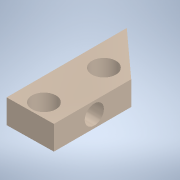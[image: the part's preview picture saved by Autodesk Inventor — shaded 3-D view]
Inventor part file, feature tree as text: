
AUTODESK INVENTOR PART (.ipt)
format: ipt  version: 2022 (Build 260153000, 153)  size: 126,464 bytes
history: native  units: mm
features: other x3, sketch x3, extrude x2, hole x1
ambient origin geometry x8: Origin, YZ Plane, XZ Plane, XY Plane, X Axis, Y Axis, Z Axis, Center Point
bodies: Body1 (feature_tree)
feature tree (9):
  other  "Твердое тело1"
  other  "РабПлоскость1"
  sketch  "Эскиз1"
  other  "РабПлоскость2"
  sketch  "Эскиз2"
  extrude  "Выдавливание1"  Depth=5.0mm TaperAngle=0.0deg
  extrude  "Выдавливание2"  Depth=7.0mm TaperAngle=0.0deg
  hole  "Отверстие1"  [1 undecoded]
  sketch  "Эскиз3"
note: 1 required parameter value undecoded (feature->parameter linkage not recoverable at this tier; creation-order binding heuristic only, values carry confidence <= 0.55)
